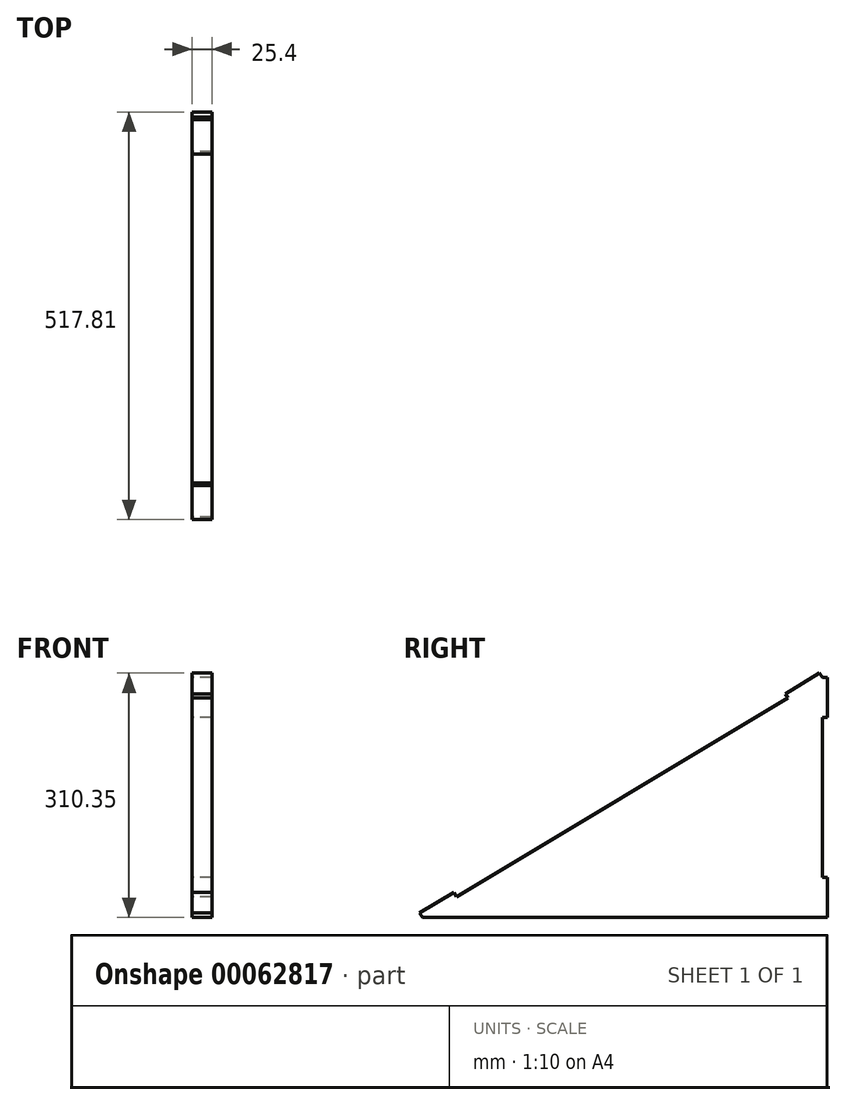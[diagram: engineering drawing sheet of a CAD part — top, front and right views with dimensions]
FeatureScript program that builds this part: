
annotation { "Feature Type Name" : "Feature", "Feature Type Description" : "" }
export const myFeature = defineFeature(function(context is Context, id is Id, definition is map)
    precondition{}
    {
        {
            var Q0;
            Q0=qCreatedBy(makeId("Right.planeOp"),FACE);
            var sketch = newSketch(context, id + "F0", { "sketchPlane" : qUnion([Q0])});
            skLineSegment(sketch, "E0", {"start": v(0, 0) * mm, "end": v(508, 0) * mm});
            skLineSegment(sketch, "E1", {"start": v(508, 0) * mm, "end": v(508, 304.8) * mm});
            skLineSegment(sketch, "E2", {"start": v(508, 304.8) * mm, "end": v(0, 0) * mm});
            skLineSegment(sketch, "E3", {"start": v(0, 0) * mm, "end": v(-3.33, 5.55) * mm});
            skLineSegment(sketch, "E4", {"start": v(-3.33, 5.55) * mm, "end": v(40.23, 31.7) * mm});
            skLineSegment(sketch, "E5", {"start": v(40.23, 31.7) * mm, "end": v(43.56, 26.14) * mm});
            skLineSegment(sketch, "E6", {"start": v(508, 304.8) * mm, "end": v(504.67, 310.35) * mm});
            skLineSegment(sketch, "E7", {"start": v(504.67, 310.35) * mm, "end": v(461.1, 284.22) * mm});
            skLineSegment(sketch, "E8", {"start": v(461.1, 284.22) * mm, "end": v(464.44, 278.66) * mm});
            skLineSegment(sketch, "E9.bottom", {"start": v(508, 0) * mm, "end": v(514.48, 0) * mm});
            skLineSegment(sketch, "E9.top", {"start": v(508, 50.8) * mm, "end": v(514.48, 50.8) * mm});
            skLineSegment(sketch, "E9.left", {"start": v(508, 0) * mm, "end": v(508, 50.8) * mm});
            skLineSegment(sketch, "E9.right", {"start": v(514.48, 0) * mm, "end": v(514.48, 50.8) * mm});
            skLineSegment(sketch, "E10.bottom", {"start": v(508, 304.8) * mm, "end": v(514.48, 304.8) * mm});
            skLineSegment(sketch, "E10.top", {"start": v(508, 254) * mm, "end": v(514.48, 254) * mm});
            skLineSegment(sketch, "E10.left", {"start": v(508, 304.8) * mm, "end": v(508, 254) * mm});
            skLineSegment(sketch, "E10.right", {"start": v(514.48, 304.8) * mm, "end": v(514.48, 254) * mm});
            skSolve(sketch);
        }
        {
            var Q0;
            Q0 = qSketchRegion(id + "F0", true);
            extrude(context, id + "F1", {"entities" : qUnion([Q0]), "depth" : 25.4 * mm});
        }
    });
